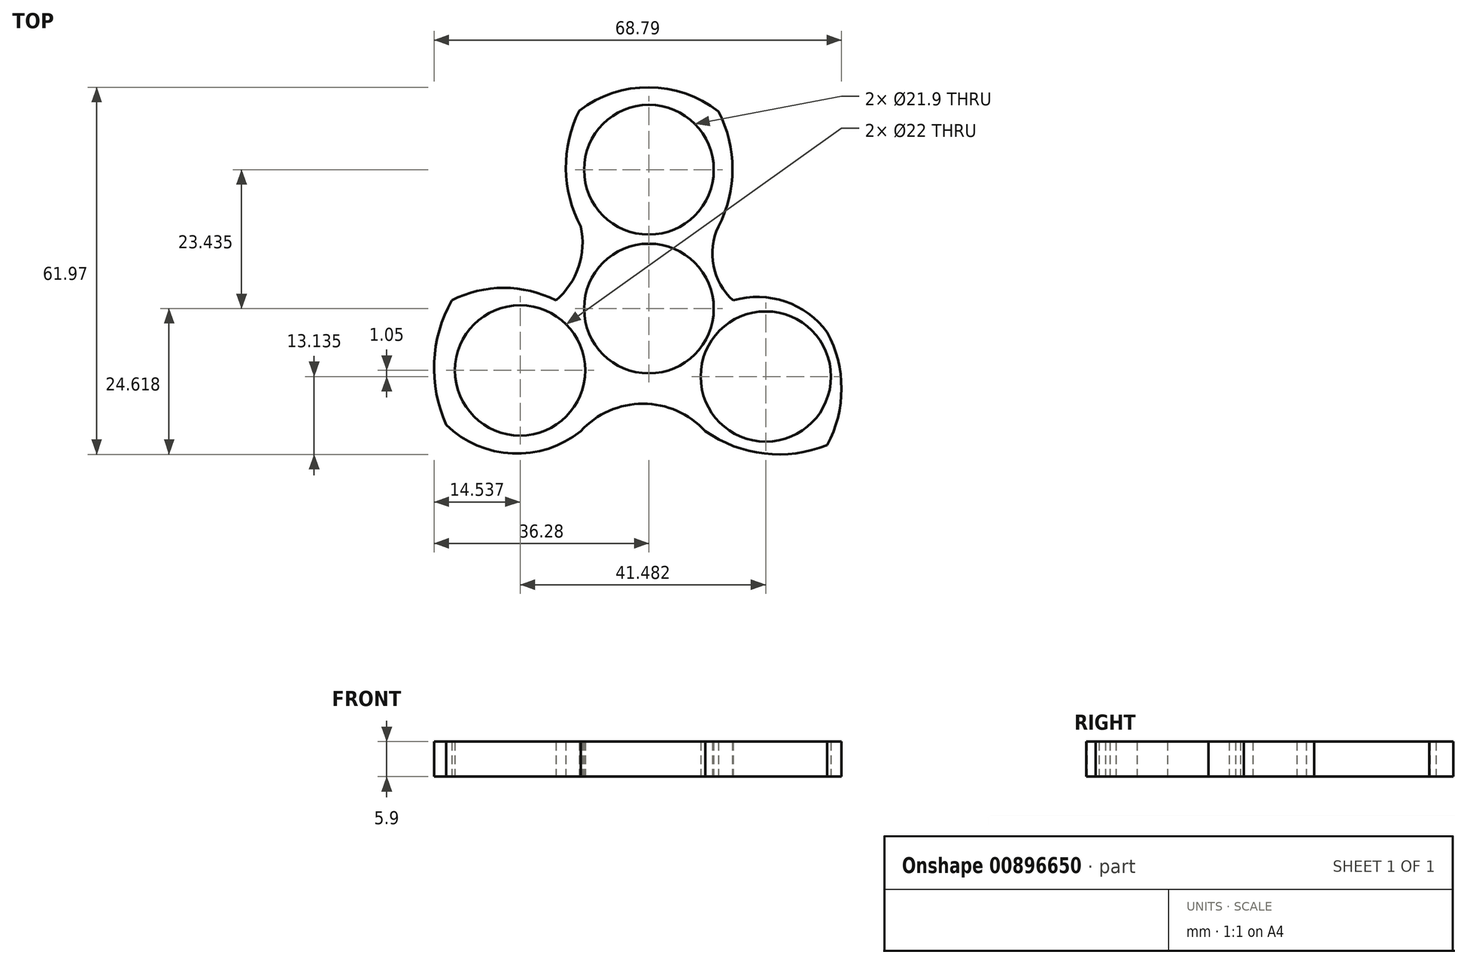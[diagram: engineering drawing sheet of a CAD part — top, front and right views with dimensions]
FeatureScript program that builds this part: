
annotation { "Feature Type Name" : "Feature", "Feature Type Description" : "" }
export const myFeature = defineFeature(function(context is Context, id is Id, definition is map)
    precondition{}
    {
        {
            var Q0;
            Q0=qCreatedBy(makeId("Top.planeOp"),FACE);
            var sketch = newSketch(context, id + "F0", { "sketchPlane" : qUnion([Q0])});
            skCircle(sketch, "E0", {"center": v(0, -1.38) * mm, "radius": 10.95 * mm});
            skCircle(sketch, "E1", {"center": v(0, 22.05) * mm, "radius": 10.95 * mm});
            skCircle(sketch, "E2", {"center": v(-21.74, -11.81) * mm, "radius": 11 * mm});
            skCircle(sketch, "E3", {"center": v(19.74, -12.86) * mm, "radius": 11 * mm});
            skArc(sketch, "E4", {"start": v(11.73, 31.9) * mm, "mid": v(0, 35.97) * mm, "end": v(-11.77, 32.03) * mm});
            skArc(sketch, "E5", {"start": v(11.73, 12.47) * mm, "mid": v(14.11, 22.18) * mm, "end": v(11.73, 31.9) * mm});
            skArc(sketch, "E6", {"start": v(11.73, 12.47) * mm, "mid": v(10.93, 5.83) * mm, "end": v(14.23, 0) * mm});
            skArc(sketch, "E7", {"start": v(30.1, -5.38) * mm, "mid": v(23.01, -0.2) * mm, "end": v(14.23, 0) * mm});
            skArc(sketch, "E8", {"start": v(30.1, -24.42) * mm, "mid": v(32.5, -14.9) * mm, "end": v(30.1, -5.38) * mm});
            skArc(sketch, "E9", {"start": v(9.5, -22.05) * mm, "mid": v(19.5, -25.86) * mm, "end": v(30.1, -24.42) * mm});
            skArc(sketch, "E10", {"start": v(9.5, -22.05) * mm, "mid": v(-1, -17.44) * mm, "end": v(-11.5, -22.05) * mm});
            skArc(sketch, "E11", {"start": v(-34.21, -21) * mm, "mid": v(-23.06, -25.85) * mm, "end": v(-11.5, -22.05) * mm});
            skArc(sketch, "E12", {"start": v(-33.3, 0) * mm, "mid": v(-36.26, -10.4) * mm, "end": v(-34.21, -21) * mm});
            skArc(sketch, "E13", {"start": v(-15.7, 0) * mm, "mid": v(-24.5, 2.12) * mm, "end": v(-33.3, 0) * mm});
            skArc(sketch, "E14", {"start": v(-15.7, 0) * mm, "mid": v(-11.86, 5.65) * mm, "end": v(-11.5, 12.47) * mm});
            skArc(sketch, "E15", {"start": v(-11.77, 32.03) * mm, "mid": v(-14.02, 22.22) * mm, "end": v(-11.5, 12.47) * mm});
            skSolve(sketch);
        }
        {
            var Q0;
            Q0=makeQuery(id+"F0.imprint","IMPRINT",FACE,{"disambiguationData":[TD([[makeQuery(id+"F0.imprint","IMPRINT",EDGE,{"derivedFrom":sQuery(id+"F0.wireOp",EDGE,"E0")}),-1.0]])]});
            extrude(context, id + "F1", {"entities" : qUnion([Q0]), "depth" : 5.9 * mm, "offsetDistance" : 25 * mm});
        }
    });
